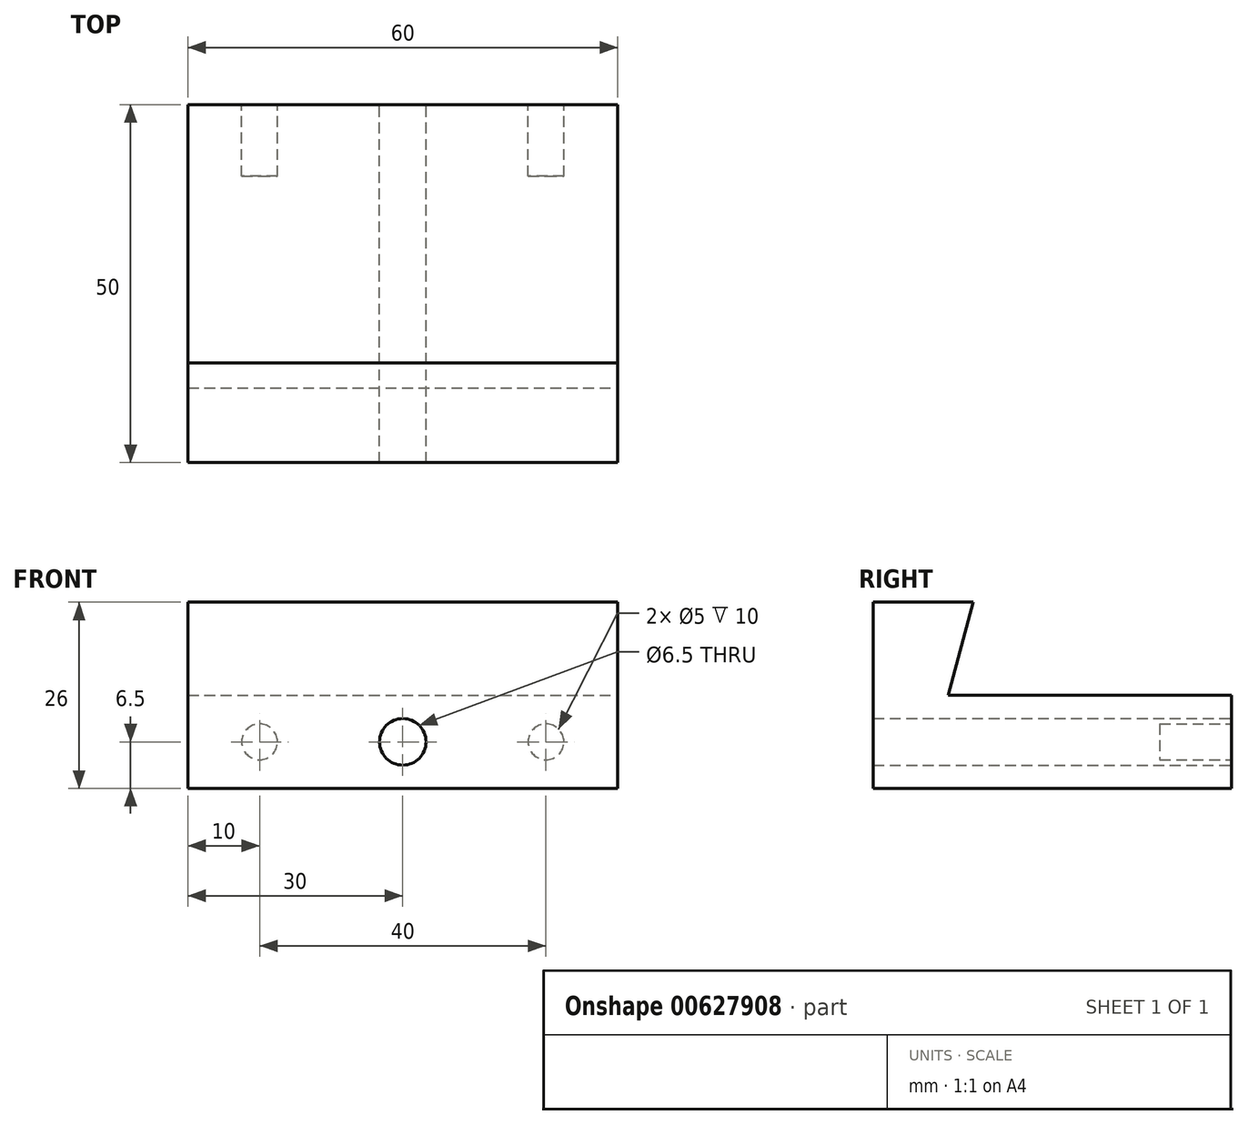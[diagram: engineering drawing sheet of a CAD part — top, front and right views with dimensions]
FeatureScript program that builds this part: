
annotation { "Feature Type Name" : "Feature", "Feature Type Description" : "" }
export const myFeature = defineFeature(function(context is Context, id is Id, definition is map)
    precondition{}
    {
        {
            var Q0;
            Q0=qCreatedBy(makeId("Top.planeOp"),FACE);
            var sketch = newSketch(context, id + "F0", { "sketchPlane" : qUnion([Q0])});
            skLineSegment(sketch, "E0.bottom", {"start": v(-30, 25) * mm, "end": v(30, 25) * mm});
            skLineSegment(sketch, "E0.top", {"start": v(-30, -25) * mm, "end": v(30, -25) * mm});
            skLineSegment(sketch, "E0.left", {"start": v(-30, 25) * mm, "end": v(-30, -25) * mm});
            skLineSegment(sketch, "E0.right", {"start": v(30, 25) * mm, "end": v(30, -25) * mm});
            skPoint(sketch, "E0.middle", {"position": v(0, 0) * mm});
            skSolve(sketch);
        }
        {
            var Q0;
            Q0=makeQuery(id+"F0.imprint","IMPRINT",FACE,{"disambiguationData":[TD([[makeQuery(id+"F0.imprint","IMPRINT",EDGE,{"derivedFrom":sQuery(id+"F0.wireOp",EDGE,"E0.bottom")}),-1.0]])]});
            extrude(context, id + "F1", {"entities" : qUnion([Q0]), "endBound" : BoundingType.SYMMETRIC, "depth" : 26 * mm, "offsetDistance" : 25 * mm});
        }
        {
            var Q0;
            Q0=makeQuery(id+"F1.opExtrude","SWEPT_FACE",FACE,{"disambiguationData":[OSD([sQuery(id+"F0.wireOp",EDGE,"E0.right")])]});
            var sketch = newSketch(context, id + "F2", { "sketchPlane" : qUnion([Q0])});
            skLineSegment(sketch, "E1", {"start": v(-14.54, 0) * mm, "end": v(-11.06, 13) * mm});
            skLineSegment(sketch, "E2", {"start": v(-14.54, 0) * mm, "end": v(25, 0) * mm});
            skLineSegment(sketch, "E3", {"start": v(25, 0) * mm, "end": v(25, 13) * mm});
            skLineSegment(sketch, "E4", {"start": v(25, 13) * mm, "end": v(-11.06, 13) * mm});
            skSolve(sketch);
        }
        {
            var Q0;
            Q0=makeQuery(id+"F2.imprint","IMPRINT",FACE,{"disambiguationData":[TD([[makeQuery(id+"F2.imprint","IMPRINT",EDGE,{"derivedFrom":sQuery(id+"F2.wireOp",EDGE,"E1")}),-1.0]])]});
            extrude(context, id + "F3", {"entities" : qUnion([Q0]), "operationType" : NewBodyOperationType.REMOVE, "oppositeDirection" : true, "depth" : 60 * mm, "offsetDistance" : 25 * mm});
        }
        {
            var Q0;
            Q0=makeQuery(id+"F1.opExtrude","SWEPT_FACE",FACE,{"disambiguationData":[OSD([sQuery(id+"F0.wireOp",EDGE,"E0.bottom")])]});
            var sketch = newSketch(context, id + "F4", { "sketchPlane" : qUnion([Q0])});
            skLineSegment(sketch, "E5", {"start": v(-30, -6.5) * mm, "end": v(30, -6.5) * mm, "construction": true});
            skCircle(sketch, "E6", {"center": v(0, -6.5) * mm, "radius": 3.25 * mm});
            skSolve(sketch);
        }
        {
            var Q0;
            Q0 = qSketchRegion(id + "F4", true);
            extrude(context, id + "F5", {"entities" : qUnion([Q0]), "operationType" : NewBodyOperationType.REMOVE, "oppositeDirection" : true, "depth" : 50 * mm, "offsetDistance" : 25 * mm});
        }
        {
            var Q0;
            Q0=makeQuery(id+"F1.opExtrude","SWEPT_FACE",FACE,{"disambiguationData":[OSD([sQuery(id+"F0.wireOp",EDGE,"E0.bottom")])]});
            var sketch = newSketch(context, id + "F6", { "sketchPlane" : qUnion([Q0])});
            skLineSegment(sketch, "E7", {"start": v(-30, -6.5) * mm, "end": v(30, -6.5) * mm, "construction": true});
            skCircle(sketch, "E8", {"center": v(-20, -6.5) * mm, "radius": 2.5 * mm});
            skCircle(sketch, "E9", {"center": v(20, -6.5) * mm, "radius": 2.5 * mm});
            skSolve(sketch);
        }
        {
            var Q0;
            Q0=makeQuery(id+"F6.imprint","IMPRINT",FACE,{"disambiguationData":[TD([[makeQuery(id+"F6.imprint","IMPRINT",EDGE,{"derivedFrom":sQuery(id+"F6.wireOp",EDGE,"E8")}),1.0]])]});
            var Q1;
            Q1=makeQuery(id+"F6.imprint","IMPRINT",FACE,{"disambiguationData":[TD([[makeQuery(id+"F6.imprint","IMPRINT",EDGE,{"derivedFrom":sQuery(id+"F6.wireOp",EDGE,"E9")}),1.0]])]});
            extrude(context, id + "F7", {"entities" : qUnion([Q0, Q1]), "operationType" : NewBodyOperationType.REMOVE, "oppositeDirection" : true, "depth" : 10 * mm, "offsetDistance" : 25 * mm});
        }
    });
